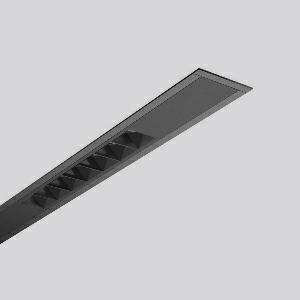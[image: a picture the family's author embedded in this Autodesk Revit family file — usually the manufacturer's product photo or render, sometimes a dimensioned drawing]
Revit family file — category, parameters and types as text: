
# Revit family: less_is_more_beamline_312472_003_c69d
name_source: partatom
category: Lighting Fixtures
units: mm (PartAtom-declared; Revit-internal decimal feet)

## family parameters
Cut with Voids When Loaded = No
Host = Face
Light Source = No
Part Type = Normal
Room Calculation Point = No
Round Connector Dimension = Use Diameter
Shared = No

## types (1)
- LESS IS MORE BEAMLINE (1 x LED Modul 930, 966.67 lm, 3000)
    Apparent Load = 35 VA
    CIE Flux Codes = 100 100 100 100 100
    Color Rendering = 90
    Color Temperature = 3000
    Default Elevation = 1800 mm
    Description = Series: LESS IS MORE BEAMLINE
Linear recessed ceiling and wall luminaire for aesthetically sophisticated lighting. Luminaire with three LED light units. Housing: extruded aluminium profile, powder-coated. End cap aluminium powder-coated. LED light unit with MRS technology: Mini-Reflector-System made of metallised thermoplastic with prismatic black glare-suppressing frame for pleasant glare-free light (RUG < 10). Each LED light unit has 7 reflector elements. Medium beam light distribution. Ceiling installation with pre-assembled SBS mounting system. LED unit with integrated converter interchangeable and removable. Suitable for through-wiring. 
Colour: deep black, matt (RAL 9005)
Length: 1702 mm
Width: 71 mm
Height: 1.5 mm
Cut-out length: 1688 mm
Cut-out width: 60 mm
Recess height: 125 mm
Luminaire: recess height: 106 mm
Lamp: LED
Socket: without socket
Colour temperature: 3000K
Colour rendering index (CRI): 90
System power: 35 W
Rated luminous flux: 2900 lm
Luminous efficiency: 83 lm/W
Control gear: Regulated power supply
Protection class: I
Type of protection: IP 20
    Height = 0 mm  [stored 0 ft]
    Lamp = 1 x LED Modul 930
    Lamp Light Flux = 966.67 lm
    Lamp count = 1
    Length = 1702 mm
    Lifetime = 50000 h
    Luminous efficacy = 83 lm/W
    Manufacturer = RZB
    ModVariant = No
    Model = 312472.003
    Mounting Place = Ceiling, Wall
    Mounting Type = Recessed
    Number of Poles = 1
    OnlyDefault = Yes
    Power Factor = 1
    Product Name = LESS IS MORE BEAMLINE
    Product group = Recessed LED linear luminaires
    ProductGroupID = 407
    Protection Class = Protection class I
    Protection Degree = IP 20
    RLX_Detail_Level = 1
    RLX_Emergency_Light_Flux = 0 lm
    RLX_Emergency_Type = 0
    RLX_Emergency_Type_DB = No
    RlxData = <blob elided: 24189 chars, md5=7ef09dac>
    Socket = socket
    Standby Power = 0 W
    System Light Flux = 2900 lm
    System Power = 35 W
    Type Comments = Product without accessories
    Type Image = 312465.003.jpg
    URL = http://relux.com
    VarID = ---
    Voltage = 230 V
    Voltage Range = 220-240 V
    Weight = 0.00 kg
    Width = 71 mm

note: [stored X ft] marks values corroborated as IEEE doubles in the binary element streams (Revit-internal decimal feet)

## geometry (parser evidence)
native form markers: Blend x4, Sweep x17
no freeform markers — native parametric forms only
